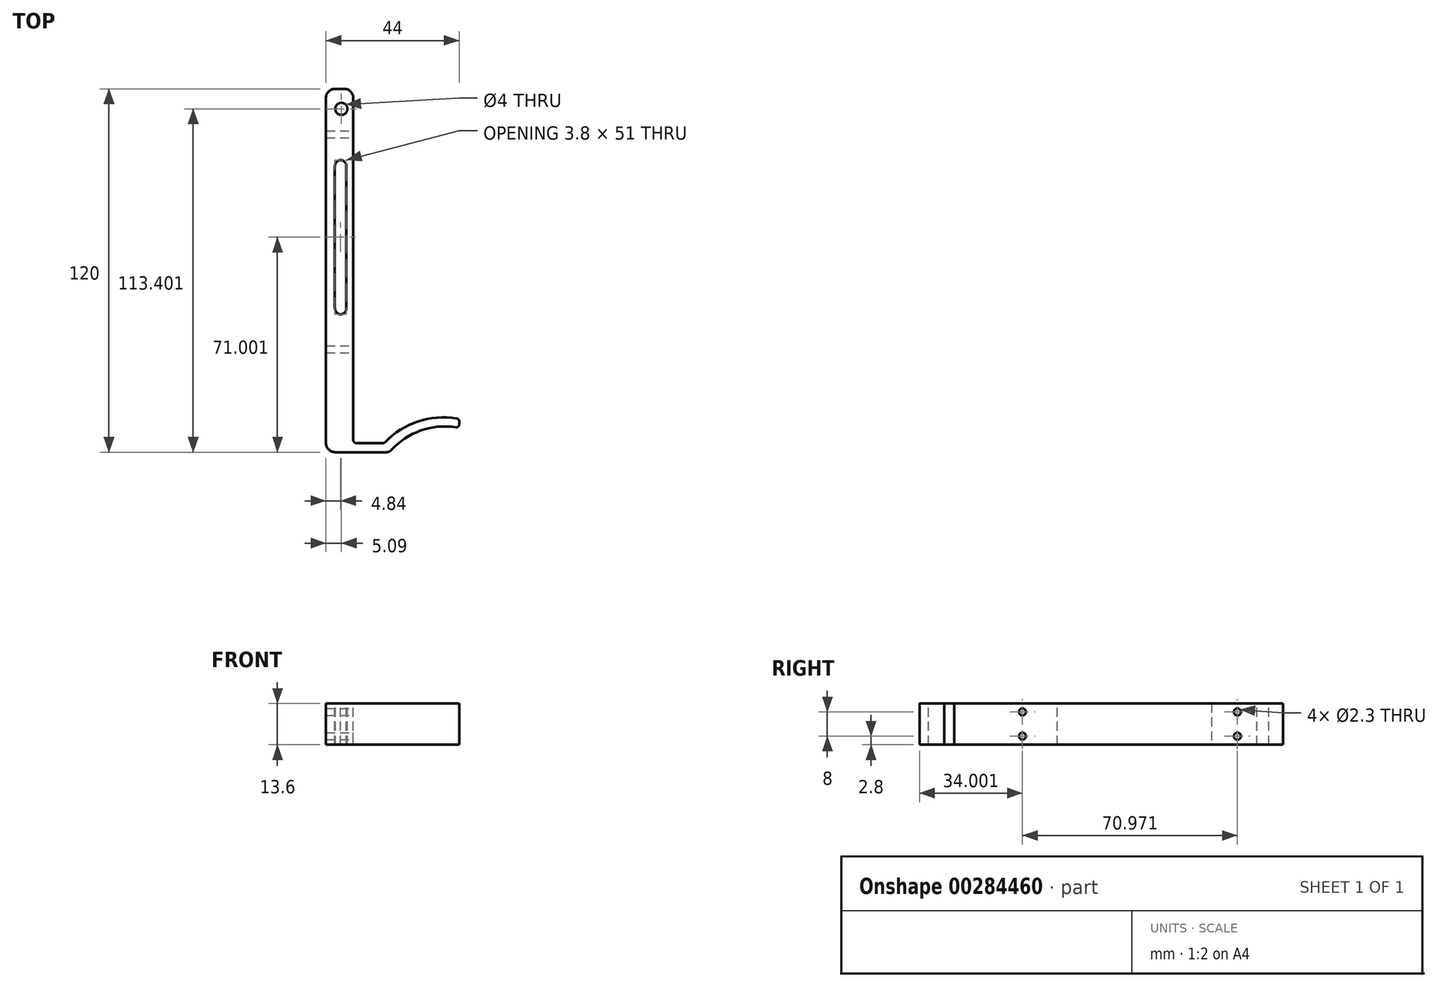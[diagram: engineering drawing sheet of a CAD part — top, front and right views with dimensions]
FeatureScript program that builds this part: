
annotation { "Feature Type Name" : "Feature", "Feature Type Description" : "" }
export const myFeature = defineFeature(function(context is Context, id is Id, definition is map)
    precondition{}
    {
        {
            var Q0;
            Q0=qCreatedBy(makeId("Top.planeOp"),FACE);
            var sketch = newSketch(context, id + "F0", { "sketchPlane" : qUnion([Q0])});
            skLineSegment(sketch, "E0.bottom", {"start": v(-0.09, 60.91) * mm, "end": v(2.91, 60.91) * mm});
            skLineSegment(sketch, "E0.top", {"start": v(-0.09, -59.09) * mm, "end": v(2.91, -59.09) * mm});
            skLineSegment(sketch, "E0.left", {"start": v(-0.09, 60.91) * mm, "end": v(-0.09, -59.09) * mm});
            skLineSegment(sketch, "E0.right", {"start": v(2.91, 60.91) * mm, "end": v(2.91, -59.09) * mm});
            skLineSegment(sketch, "E1.left", {"start": v(2.91, -59.09) * mm, "end": v(2.91, -56.09) * mm});
            skLineSegment(sketch, "E2", {"start": v(2.91, -56.09) * mm, "end": v(13.11, -56.09) * mm});
            skArc(sketch, "E3", {"start": v(37.91, -48.09) * mm, "mid": v(24.49, -48.91) * mm, "end": v(13.11, -56.09) * mm});
            skLineSegment(sketch, "E4", {"start": v(2.91, -59.09) * mm, "end": v(14.91, -59.09) * mm});
            skArc(sketch, "E5", {"start": v(37.91, -51.09) * mm, "mid": v(25.3, -51.92) * mm, "end": v(14.91, -59.09) * mm});
            skLineSegment(sketch, "E6", {"start": v(37.91, -48.09) * mm, "end": v(37.91, -51.09) * mm});
            skLineSegment(sketch, "E7.bottom", {"start": v(-0.09, 60.91) * mm, "end": v(-6.09, 60.91) * mm});
            skLineSegment(sketch, "E7.top", {"start": v(-0.09, -59.09) * mm, "end": v(-6.09, -59.09) * mm});
            skLineSegment(sketch, "E7.right", {"start": v(-6.09, 60.91) * mm, "end": v(-6.09, -59.09) * mm});
            skSolve(sketch);
        }
        {
            var Q0;
            Q0 = qSketchRegion(id + "F0", true);
            extrude(context, id + "F1", {"entities" : qUnion([Q0]), "oppositeDirection" : true, "depth" : 12.8 * mm, "hasSecondDirection" : true, "secondDirectionOppositeDirection" : false, "secondDirectionDepth" : .8 * mm});
        }
        {
            var Q0;
            Q0=makeQuery(id+"F1.opExtrude","SWEPT_EDGE",EDGE,{"disambiguationData":[OSD([sQuery(id+"F0.wireOp",EDGE,"E4"),sQuery(id+"F0.wireOp",EDGE,"E5")])]});
            var Q1;
            Q1=makeQuery(id+"F1.opExtrude","SWEPT_EDGE",EDGE,{"disambiguationData":[OSD([sQuery(id+"F0.wireOp",EDGE,"E0.top"),sQuery(id+"F0.wireOp",EDGE,"E0.left")])]});
            fillet(context, id + "F2", {"entities" : qUnion([Q0, Q1]), "radius" : 2 * mm, "tangentPropagation" : true, "allowEdgeOverflow" : false});
        }
        {
            var Q0;
            Q0=makeQuery(id+"F1.opExtrude","SWEPT_EDGE",EDGE,{"disambiguationData":[OSD([sQuery(id+"F0.wireOp",EDGE,"E0.right"),sQuery(id+"F0.wireOp",EDGE,"E1.left"),sQuery(id+"F0.wireOp",EDGE,"E2")])]});
            var Q1;
            Q1=makeQuery(id+"F1.opExtrude","SWEPT_EDGE",EDGE,{"disambiguationData":[OSD([sQuery(id+"F0.wireOp",EDGE,"E2"),sQuery(id+"F0.wireOp",EDGE,"E3")])]});
            var Q2;
            Q2=makeQuery(id+"F1.opExtrude","SWEPT_EDGE",EDGE,{"disambiguationData":[OSD([sQuery(id+"F0.wireOp",EDGE,"E3"),sQuery(id+"F0.wireOp",EDGE,"E6")])]});
            var Q3;
            Q3=makeQuery(id+"F1.opExtrude","SWEPT_EDGE",EDGE,{"disambiguationData":[OSD([sQuery(id+"F0.wireOp",EDGE,"E5"),sQuery(id+"F0.wireOp",EDGE,"E6")])]});
            fillet(context, id + "F3", {"entities" : qUnion([Q0, Q1, Q2, Q3]), "radius" : 1 * mm, "tangentPropagation" : true, "allowEdgeOverflow" : false});
        }
        {
            var Q0;
            Q0=makeQuery(id+"F1.opExtrude","SWEPT_FACE",FACE,{"disambiguationData":[OSD([sQuery(id+"F0.wireOp",EDGE,"E0.right")])]});
            var sketch = newSketch(context, id + "F4", { "sketchPlane" : qUnion([Q0])});
            skCircle(sketch, "E8", {"center": v(-25.09, -10) * mm, "radius": 1.15 * mm});
            skCircle(sketch, "E9", {"center": v(-25.09, -2) * mm, "radius": 1.15 * mm});
            skCircle(sketch, "E10", {"center": v(45.88, -2) * mm, "radius": 1.15 * mm});
            skCircle(sketch, "E11", {"center": v(45.88, -10) * mm, "radius": 1.15 * mm});
            skSolve(sketch);
        }
        {
            var Q0;
            Q0=makeQuery(id+"F4.imprint","IMPRINT",FACE,{"disambiguationData":[TD([[makeQuery(id+"F4.imprint","IMPRINT",EDGE,{"derivedFrom":sQuery(id+"F4.wireOp",EDGE,"E9")}),1.0]])]});
            var Q1;
            Q1=makeQuery(id+"F4.imprint","IMPRINT",FACE,{"disambiguationData":[TD([[makeQuery(id+"F4.imprint","IMPRINT",EDGE,{"derivedFrom":sQuery(id+"F4.wireOp",EDGE,"E8")}),1.0]])]});
            var Q2;
            Q2=makeQuery(id+"F4.imprint","IMPRINT",FACE,{"disambiguationData":[TD([[makeQuery(id+"F4.imprint","IMPRINT",EDGE,{"derivedFrom":sQuery(id+"F4.wireOp",EDGE,"E10")}),1.0]])]});
            var Q3;
            Q3=makeQuery(id+"F4.imprint","IMPRINT",FACE,{"disambiguationData":[TD([[makeQuery(id+"F4.imprint","IMPRINT",EDGE,{"derivedFrom":sQuery(id+"F4.wireOp",EDGE,"E11")}),1.0]])]});
            var Q4;
            Q4=sQuery(id+"F4.wireOp",EDGE,"E10");
            var Q5;
            Q5=sQuery(id+"F4.wireOp",EDGE,"E11");
            var Q6;
            Q6=sQuery(id+"F4.wireOp",EDGE,"E9");
            var Q7;
            Q7=sQuery(id+"F4.wireOp",EDGE,"E8");
            extrude(context, id + "F5", {"entities" : qUnion([Q0, Q1, Q2, Q3]), "operationType" : NewBodyOperationType.REMOVE, "surfaceEntities" : qUnion([Q4, Q5, Q6, Q7]), "oppositeDirection" : true, "depth" : 15 * mm});
        }
        {
            var Q0;
            Q0=makeQuery(id+"F1.opExtrude","CAP_FACE",FACE,{"disambiguationData":[OSD([sQuery(id+"F0.wireOp",EDGE,"E0.bottom"),sQuery(id+"F0.wireOp",EDGE,"E0.top"),sQuery(id+"F0.wireOp",EDGE,"E0.left"),sQuery(id+"F0.wireOp",EDGE,"E0.right"),sQuery(id+"F0.wireOp",EDGE,"E2"),sQuery(id+"F0.wireOp",EDGE,"E3"),sQuery(id+"F0.wireOp",EDGE,"E4"),sQuery(id+"F0.wireOp",EDGE,"E5"),sQuery(id+"F0.wireOp",EDGE,"E6"),sQuery(id+"F0.wireOp",EDGE,"E7.bottom"),sQuery(id+"F0.wireOp",EDGE,"E7.top"),sQuery(id+"F0.wireOp",EDGE,"E7.right")])],"isStart":true});
            var sketch = newSketch(context, id + "F6", { "sketchPlane" : qUnion([Q0])});
            skLineSegment(sketch, "E12.bottom", {"start": v(0.65, 37.41) * mm, "end": v(-3.15, 37.41) * mm});
            skLineSegment(sketch, "E12.top", {"start": v(0.65, -13.59) * mm, "end": v(-3.15, -13.59) * mm});
            skLineSegment(sketch, "E12.left", {"start": v(0.65, 37.41) * mm, "end": v(0.65, -13.59) * mm});
            skLineSegment(sketch, "E12.right", {"start": v(-3.15, 37.41) * mm, "end": v(-3.15, -13.59) * mm});
            skCircle(sketch, "E13", {"center": v(-1, 54.31) * mm, "radius": 2 * mm});
            skSolve(sketch);
        }
        {
            var Q0;
            Q0 = qSketchRegion(id + "F6", true);
            extrude(context, id + "F7", {"entities" : qUnion([Q0]), "operationType" : NewBodyOperationType.REMOVE, "oppositeDirection" : true, "depth" : 19 * mm});
        }
        {
            var Q0;
            Q0=makeQuery(id+"F1.opExtrude","SWEPT_EDGE",EDGE,{"disambiguationData":[OSD([sQuery(id+"F0.wireOp",EDGE,"E7.bottom"),sQuery(id+"F0.wireOp",EDGE,"E7.right")])]});
            var Q1;
            Q1=makeQuery(id+"F1.opExtrude","SWEPT_EDGE",EDGE,{"disambiguationData":[OSD([sQuery(id+"F0.wireOp",EDGE,"E0.bottom"),sQuery(id+"F0.wireOp",EDGE,"E0.right")])]});
            var Q2;
            Q2=makeQuery(id+"F1.opExtrude","SWEPT_EDGE",EDGE,{"disambiguationData":[OSD([sQuery(id+"F0.wireOp",EDGE,"E7.top"),sQuery(id+"F0.wireOp",EDGE,"E7.right")])]});
            fillet(context, id + "F8", {"entities" : qUnion([Q0, Q1, Q2]), "radius" : 3 * mm, "tangentPropagation" : true, "allowEdgeOverflow" : false});
        }
        {
            var Q0;
            Q0=makeQuery(id+"F7.boolean.opBoolean","COPY",EDGE,{"derivedFrom":makeQuery(id+"F7.opExtrude","SWEPT_EDGE",EDGE,{"disambiguationData":[OSD([sQuery(id+"F6.wireOp",EDGE,"E12.bottom"),sQuery(id+"F6.wireOp",EDGE,"E12.right")])]})});
            var Q1;
            Q1=makeQuery(id+"F7.boolean.opBoolean","COPY",EDGE,{"derivedFrom":makeQuery(id+"F7.opExtrude","SWEPT_EDGE",EDGE,{"disambiguationData":[OSD([sQuery(id+"F6.wireOp",EDGE,"E12.bottom"),sQuery(id+"F6.wireOp",EDGE,"E12.left")])]})});
            var Q2;
            Q2=makeQuery(id+"F7.boolean.opBoolean","COPY",EDGE,{"derivedFrom":makeQuery(id+"F7.opExtrude","SWEPT_EDGE",EDGE,{"disambiguationData":[OSD([sQuery(id+"F6.wireOp",EDGE,"E12.top"),sQuery(id+"F6.wireOp",EDGE,"E12.right")])]})});
            var Q3;
            Q3=makeQuery(id+"F7.boolean.opBoolean","COPY",EDGE,{"derivedFrom":makeQuery(id+"F7.opExtrude","SWEPT_EDGE",EDGE,{"disambiguationData":[OSD([sQuery(id+"F6.wireOp",EDGE,"E12.top"),sQuery(id+"F6.wireOp",EDGE,"E12.left")])]})});
            fillet(context, id + "F9", {"entities" : qUnion([Q0, Q1, Q2, Q3]), "radius" : 2 * mm, "tangentPropagation" : true, "allowEdgeOverflow" : false});
        }
    });
